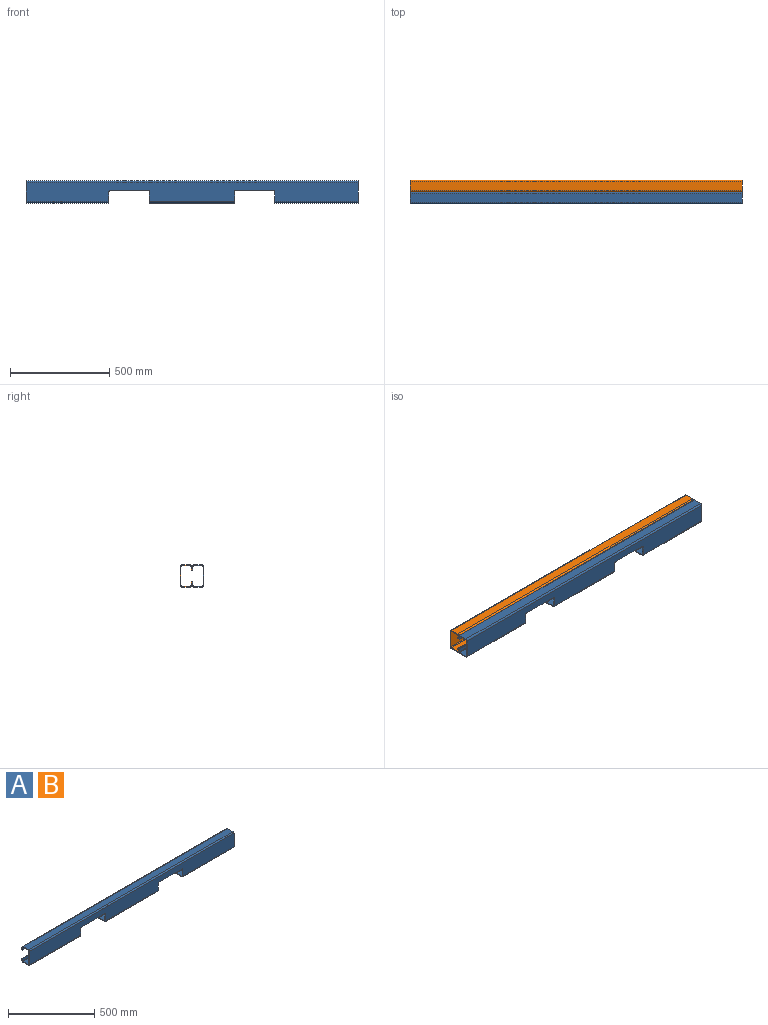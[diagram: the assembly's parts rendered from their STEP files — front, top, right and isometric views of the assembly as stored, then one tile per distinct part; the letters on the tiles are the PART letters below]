
ASSEMBLY  parts=2 mates=1
PART A: 82 faces, bbox 1676.4x60.3x111.1 mm
  f0: plane 44.45x4.76mm, normal (-1,0,0), area 211.7mm2, adj f2,f3,f30,f78
  f1: plane 44.45x4.76mm, normal (1,0,0), area 211.7mm2, adj f2,f3,f31,f79
  f2: plane 419.1x44.45mm, normal (0,0,-1), area 18629mm2, adj f0,f1,f32,f80
  f3: plane 419.1x44.45mm, normal (0,0,1), area 18629mm2, adj f0,f1,f33,f81
  f4: plane 44.45x4.76mm, normal (1,0,0), area 211.7mm2, adj f6,f7,f35,f70
  f5: plane 44.45x4.76mm, normal (-1,0,0), area 211.7mm2, adj f6,f7,f34,f69
  f6: plane 419.1x44.45mm, normal (0,0,-1), area 18629mm2, adj f4,f5,f36,f71
  f7: plane 419.1x44.45mm, normal (0,0,1), area 18629mm2, adj f4,f5,f37,f72
  f8: plane 44.45x4.76mm, normal (-1,0,0), area 211.7mm2, adj f10,f11,f42,f60
  f9: plane 44.45x4.76mm, normal (1,0,0), area 211.7mm2, adj f10,f11,f43,f61
  f10: plane 431.8x44.45mm, normal (0,0,-1), area 19193.5mm2, adj f8,f9,f44,f62
  f11: plane 431.8x44.45mm, normal (0,0,1), area 19193.5mm2, adj f8,f9,f45,f63
  f12: plane 44.45x4.76mm, normal (1,0,0), area 211.7mm2, adj f14,f15,f39,f52
  f13: plane 44.45x4.76mm, normal (-1,0,0), area 211.7mm2, adj f14,f15,f38,f51
  f14: plane 1676.4x44.45mm, normal (0,0,1), area 74516mm2, adj f12,f13,f40,f53
  f15: plane 1676.4x44.45mm, normal (0,0,-1), area 74516mm2, adj f12,f13,f41,f54
  f16: cylinder r=6.35mm len=6.35mm, axis (0,-1,0), area 47.5mm2, adj f17,f27,f28,f29
  f17: plane 190.5x4.76mm, normal (0,0,-1), area 907.3mm2, adj f16,f18,f28,f29
  f18: cylinder r=6.35mm len=6.35mm, axis (0,-1,0), area 47.5mm2, adj f17,f19,f28,f29
  f19: plane 49.21x4.76mm, normal (-1,0,0), area 234.4mm2, adj f18,f28,f29,f34
  f20: plane 95.25x4.76mm, normal (1,0,0), area 453.6mm2, adj f28,f29,f35,f39
  f21: plane 95.25x4.76mm, normal (-1,0,0), area 453.6mm2, adj f28,f29,f30,f38
  f22: plane 49.21x4.76mm, normal (1,0,0), area 234.4mm2, adj f23,f28,f29,f31
  f23: cylinder r=6.35mm len=6.35mm, axis (0,-1,0), area 47.5mm2, adj f22,f24,f28,f29
  f24: plane 190.5x4.76mm, normal (0,0,-1), area 907.3mm2, adj f23,f25,f28,f29
  f25: cylinder r=6.35mm len=6.35mm, axis (0,-1,0), area 47.5mm2, adj f24,f26,f28,f29
  f26: plane 49.21x4.76mm, normal (-1,0,0), area 234.4mm2, adj f25,f28,f29,f42
  f27: plane 49.21x4.76mm, normal (1,0,0), area 234.4mm2, adj f16,f28,f29,f43
  f28: plane 1676.4x95.25mm, normal (0,-1,0), area 137131.1mm2, adj f16,f17,f18,f19,f20,f21,f22,f23
  f29: plane 1676.4x95.25mm, normal (0,1,0), area 137131.1mm2, adj f16,f17,f18,f19,f20,f21,f22,f23
  f30: plane 7.94x7.94mm, normal (-1,0,0), area 41.6mm2, adj f0,f21,f32,f33
  f31: plane 7.94x7.94mm, normal (1,0,0), area 41.6mm2, adj f1,f22,f32,f33
  f32: cylinder r=7.94mm len=419.1mm, axis (-1,0,0), area 5225.4mm2, adj f2,f28,f30,f31
  f33: cylinder r=3.17mm len=419.1mm, axis (-1,0,0), area 2090.2mm2, adj f3,f29,f30,f31
  f34: plane 7.94x7.94mm, normal (-1,0,0), area 41.6mm2, adj f5,f19,f36,f37
  f35: plane 7.94x7.94mm, normal (1,0,0), area 41.6mm2, adj f4,f20,f36,f37
  f36: cylinder r=7.94mm len=419.1mm, axis (-1,0,0), area 5225.4mm2, adj f6,f28,f34,f35
  f37: cylinder r=3.17mm len=419.1mm, axis (-1,0,0), area 2090.2mm2, adj f7,f29,f34,f35
  f38: plane 7.94x7.94mm, normal (-1,0,0), area 41.6mm2, adj f13,f21,f40,f41
  f39: plane 7.94x7.94mm, normal (1,0,0), area 41.6mm2, adj f12,f20,f40,f41
  f40: cylinder r=7.94mm len=1676.4mm, axis (-1,0,0), area 20901.7mm2, adj f14,f28,f38,f39
  f41: cylinder r=3.17mm len=1676.4mm, axis (-1,0,0), area 8360.7mm2, adj f15,f29,f38,f39
  f42: plane 7.94x7.94mm, normal (-1,0,0), area 41.6mm2, adj f8,f26,f44,f45
  f43: plane 7.94x7.94mm, normal (1,0,0), area 41.6mm2, adj f9,f27,f44,f45
  f44: cylinder r=7.94mm len=431.8mm, axis (-1,0,0), area 5383.8mm2, adj f10,f28,f42,f43
  f45: cylinder r=3.17mm len=431.8mm, axis (-1,0,0), area 2153.5mm2, adj f11,f29,f42,f43
  f46: plane 17.46x4.76mm, normal (-1,0,0), area 83.2mm2, adj f48,f49,f50,f51
  f47: plane 17.46x4.76mm, normal (1,0,0), area 83.2mm2, adj f48,f49,f50,f52
  f48: plane 1676.4x4.76mm, normal (0,0,-1), area 7983.9mm2, adj f46,f47,f49,f50
  f49: plane 1676.4x17.46mm, normal (0,1,0), area 29274.1mm2, adj f46,f47,f48,f53
  f50: plane 1676.4x17.46mm, normal (0,-1,0), area 29274.1mm2, adj f46,f47,f48,f54
  f51: plane 7.94x7.94mm, normal (-1,0,0), area 41.6mm2, adj f13,f46,f53,f54
  f52: plane 7.94x7.94mm, normal (1,0,0), area 41.6mm2, adj f12,f47,f53,f54
  f53: cylinder r=7.94mm len=1676.4mm, axis (-1,0,0), area 20901.7mm2, adj f14,f49,f51,f52
  f54: cylinder r=3.17mm len=1676.4mm, axis (-1,0,0), area 8360.7mm2, adj f15,f50,f51,f52
  f55: plane 17.46x4.76mm, normal (-1,0,0), area 83.2mm2, adj f56,f58,f59,f60
  f56: plane 431.8x4.76mm, normal (0,0,1), area 2056.4mm2, adj f55,f57,f58,f59
  f57: plane 17.46x4.76mm, normal (1,0,0), area 83.2mm2, adj f56,f58,f59,f61
  f58: plane 431.8x17.46mm, normal (0,1,0), area 7540.3mm2, adj f55,f56,f57,f62
  f59: plane 431.8x17.46mm, normal (0,-1,0), area 7540.3mm2, adj f55,f56,f57,f63
  f60: plane 7.94x7.94mm, normal (-1,0,0), area 41.6mm2, adj f8,f55,f62,f63
  f61: plane 7.94x7.94mm, normal (1,0,0), area 41.6mm2, adj f9,f57,f62,f63
  f62: cylinder r=7.94mm len=431.8mm, axis (-1,0,0), area 5383.8mm2, adj f10,f58,f60,f61
  f63: cylinder r=3.17mm len=431.8mm, axis (-1,0,0), area 2153.5mm2, adj f11,f59,f60,f61
  f64: plane 419.1x4.76mm, normal (0,0,1), area 1996mm2, adj f65,f66,f67,f68
  f65: plane 17.46x4.76mm, normal (1,0,0), area 83.2mm2, adj f64,f67,f68,f70
  f66: plane 17.46x4.76mm, normal (-1,0,0), area 83.2mm2, adj f64,f67,f68,f69
  f67: plane 419.1x17.46mm, normal (0,1,0), area 7318.5mm2, adj f64,f65,f66,f71
  f68: plane 419.1x17.46mm, normal (0,-1,0), area 7318.5mm2, adj f64,f65,f66,f72
  f69: plane 7.94x7.94mm, normal (-1,0,0), area 41.6mm2, adj f5,f66,f71,f72
  f70: plane 7.94x7.94mm, normal (1,0,0), area 41.6mm2, adj f4,f65,f71,f72
  f71: cylinder r=7.94mm len=419.1mm, axis (-1,0,0), area 5225.4mm2, adj f6,f67,f69,f70
  f72: cylinder r=3.17mm len=419.1mm, axis (-1,0,0), area 2090.2mm2, adj f7,f68,f69,f70
  f73: plane 17.46x4.76mm, normal (-1,0,0), area 83.2mm2, adj f74,f76,f77,f78
  f74: plane 419.1x4.76mm, normal (0,0,1), area 1996mm2, adj f73,f75,f76,f77
  f75: plane 17.46x4.76mm, normal (1,0,0), area 83.2mm2, adj f74,f76,f77,f79
  f76: plane 419.1x17.46mm, normal (0,1,0), area 7318.5mm2, adj f73,f74,f75,f80
  f77: plane 419.1x17.46mm, normal (0,-1,0), area 7318.5mm2, adj f73,f74,f75,f81
  f78: plane 7.94x7.94mm, normal (-1,0,0), area 41.6mm2, adj f0,f73,f80,f81
  f79: plane 7.94x7.94mm, normal (1,0,0), area 41.6mm2, adj f1,f75,f80,f81
  f80: cylinder r=7.94mm len=419.1mm, axis (-1,0,0), area 5225.4mm2, adj f2,f76,f78,f79
  f81: cylinder r=3.17mm len=419.1mm, axis (-1,0,0), area 2090.2mm2, adj f3,f77,f78,f79
PART B: same geometry as A
PLACE A at identity
PLACE B rot(axis=(0,0,1),180deg) t=(0,60.33,0)mm
MATE fastened B.f49 <-> A.f49  axis (0,-1,0) through (0,30.16,47.63)mm
